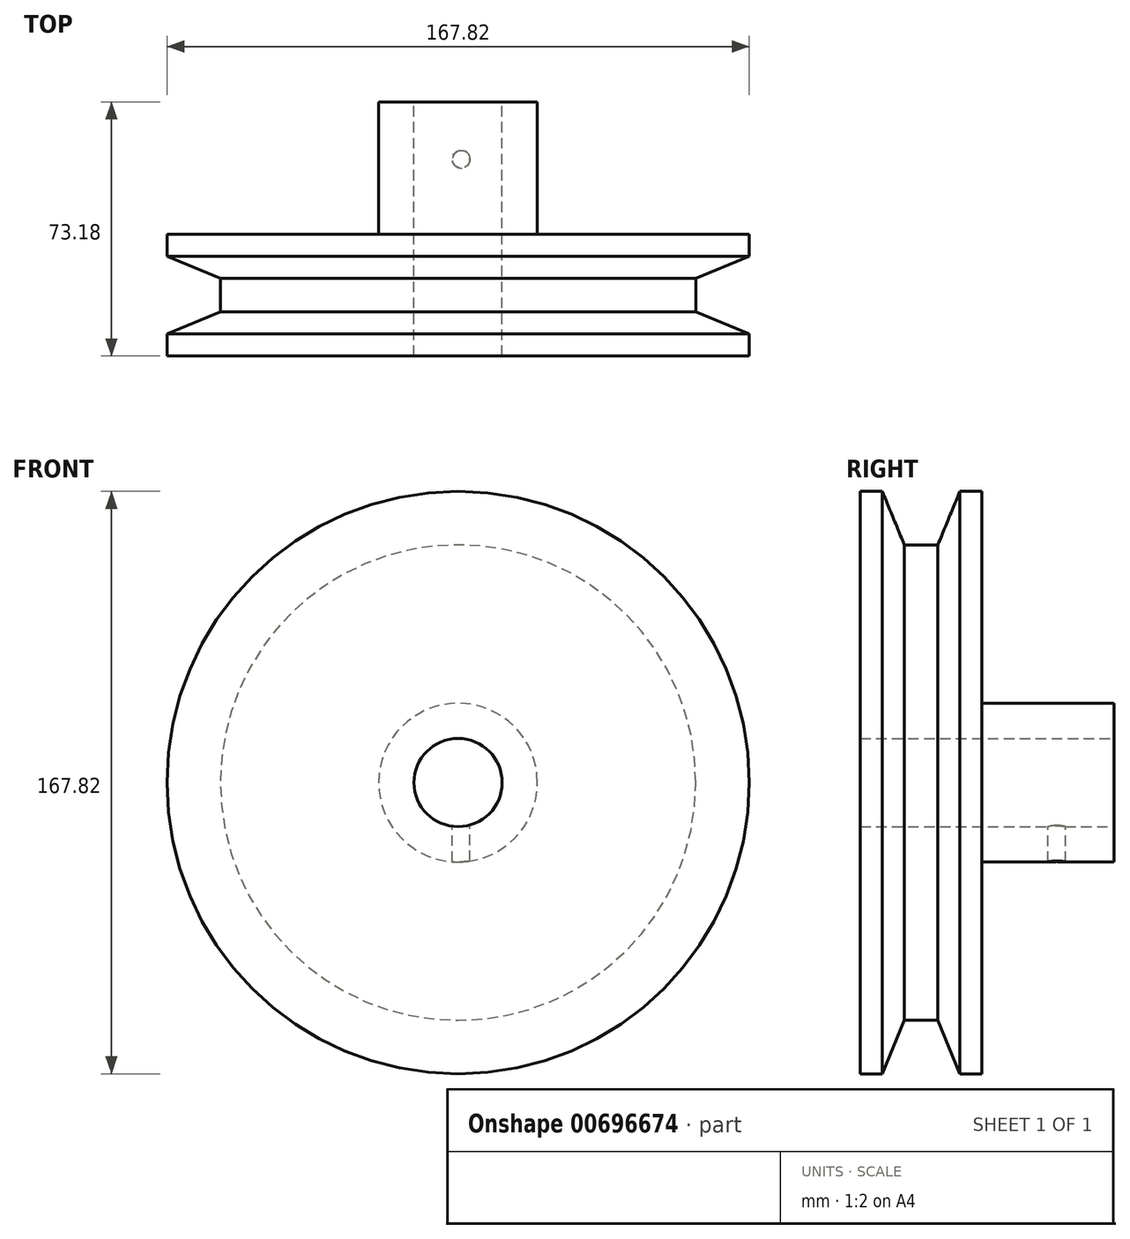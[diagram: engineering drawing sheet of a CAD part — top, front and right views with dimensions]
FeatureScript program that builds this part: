
annotation { "Feature Type Name" : "Feature", "Feature Type Description" : "" }
export const myFeature = defineFeature(function(context is Context, id is Id, definition is map)
    precondition{}
    {
        {
            var Q0;
            Q0=qCreatedBy(makeId("Top.planeOp"),FACE);
            var sketch = newSketch(context, id + "F0", { "sketchPlane" : qUnion([Q0])});
            skLineSegment(sketch, "E0.bottom", {"start": v(0, 12.25) * mm, "end": v(71.21, 12.25) * mm});
            skLineSegment(sketch, "E0.top", {"start": v(0, -10.13) * mm, "end": v(71.21, -10.13) * mm});
            skLineSegment(sketch, "E0.left", {"start": v(0, 12.25) * mm, "end": v(0, -10.13) * mm});
            skLineSegment(sketch, "E1", {"start": v(71.21, 12.25) * mm, "end": v(55.79, 5.9) * mm});
            skLineSegment(sketch, "E2", {"start": v(55.79, 5.9) * mm, "end": v(55.79, -3.78) * mm});
            skLineSegment(sketch, "E3", {"start": v(55.79, -3.78) * mm, "end": v(71.21, -10.13) * mm});
            skSolve(sketch);
        }
        {
            var Q0;
            Q0=qCreatedBy(makeId("Front.planeOp"),FACE);
            var sketch = newSketch(context, id + "F1", { "sketchPlane" : qUnion([Q0])});
            skCircle(sketch, "E4", {"center": v(-12.7, -0.33) * mm, "radius": 12.7 * mm});
            skPoint(sketch, "E4.first.point", {"position": v(0, 0) * mm});
            skPoint(sketch, "E4.second.point", {"position": v(-25.4, 0) * mm});
            skPoint(sketch, "E4.third.point", {"position": v(-6.22, 10.6) * mm});
            skSolve(sketch);
        }
        {
            var Q0;
            Q0=makeQuery(id+"F0.imprint","IMPRINT",FACE,{"disambiguationData":[TD([[makeQuery(id+"F0.imprint","IMPRINT",EDGE,{"derivedFrom":sQuery(id+"F0.wireOp",EDGE,"E0.bottom")}),-1.0]])]});
            var Q1;
            Q1=sQuery(id+"F1.wireOp",EDGE,"E4");
            revolve(context, id + "F2", {"entities" : qUnion([Q0]), "axis" : qUnion([Q1]), "revolveType" : RevolveType.FULL});
        }
        {
            var Q0;
            Q0=makeQuery(id+"F2.opRevolve","SWEPT_FACE",FACE,{"disambiguationData":[OSD([sQuery(id+"F0.wireOp",EDGE,"E0.bottom")])]});
            extrude(context, id + "F3", {"entities" : qUnion([Q0]), "operationType" : NewBodyOperationType.ADD, "depth" : 6.35 * mm, "offsetDistance" : 25.4 * mm});
        }
        {
            var Q0;
            Q0=makeQuery(id+"F2.opRevolve","SWEPT_FACE",FACE,{"disambiguationData":[OSD([sQuery(id+"F0.wireOp",EDGE,"E0.top")])]});
            extrude(context, id + "F4", {"entities" : qUnion([Q0]), "operationType" : NewBodyOperationType.ADD, "depth" : 6.35 * mm, "offsetDistance" : 25.4 * mm});
        }
        {
            var Q0;
            Q0=makeQuery(id+"F3.opExtrude","CAP_FACE",FACE,{"disambiguationData":[OSD([sQuery(id+"F0.wireOp",EDGE,"E0.bottom")])],"isStart":false});
            var sketch = newSketch(context, id + "F5", { "sketchPlane" : qUnion([Q0])});
            skCircle(sketch, "E5", {"center": v(12.7, -0.33) * mm, "radius": 22.86 * mm});
            skSolve(sketch);
        }
        {
            var Q0;
            Q0=makeQuery(id+"F5.imprint","IMPRINT",FACE,{"disambiguationData":[TD([[makeQuery(id+"F5.imprint","IMPRINT",EDGE,{"derivedFrom":sQuery(id+"F5.wireOp",EDGE,"E5")}),1.0]])]});
            extrude(context, id + "F6", {"entities" : qUnion([Q0]), "operationType" : NewBodyOperationType.ADD, "depth" : 38.1 * mm, "offsetDistance" : 25.4 * mm});
        }
        {
            var Q0;
            Q0=qCreatedBy(makeId("Top.planeOp"),FACE);
            var sketch = newSketch(context, id + "F7", { "sketchPlane" : qUnion([Q0])});
            skPoint(sketch, "E6", {"position": v(-11.82, 40.2) * mm});
            skSolve(sketch);
        }
        {
            var Q0;
            Q0=sQuery(id+"F7.wireOp",VERTEX,"E6");
            var Q1;
            Q1=makeQuery(id+"F2.opRevolve","SWEPT_BODY",BODY,{"disambiguationData":[OSD([sQuery(id+"F0.wireOp",EDGE,"E0.bottom"),sQuery(id+"F0.wireOp",EDGE,"E0.top"),sQuery(id+"F0.wireOp",EDGE,"E0.left"),sQuery(id+"F0.wireOp",EDGE,"E1"),sQuery(id+"F0.wireOp",EDGE,"E2"),sQuery(id+"F0.wireOp",EDGE,"E3")])]});
            hole(context, id + "F8", {"style" : HoleStyle.SIMPLE, "endStyle" : HoleEndStyle.THROUGH, "standardTappedOrClearance" : lookupTablePath({ "standard" : "ANSI", "engagement" : "75%", "pitch" : "20 tpi", "size" : "1/4", "type" : "Tapped" }), "standardBlindInLast" : lookupTablePath({ "standard" : "ANSI", "engagement" : "75%", "pitch" : "20 tpi", "size" : "1/4", "type" : "Tapped" }), "holeDiameter" : 5.1 * mm, "majorDiameter" : 6.35 * mm, "showTappedDepth" : true, "tappedDepth" : 5.08 * mm, "tapClearance" : 3, "locations" : qUnion([Q0]), "scope" : qUnion([Q1])});
        }
    });
